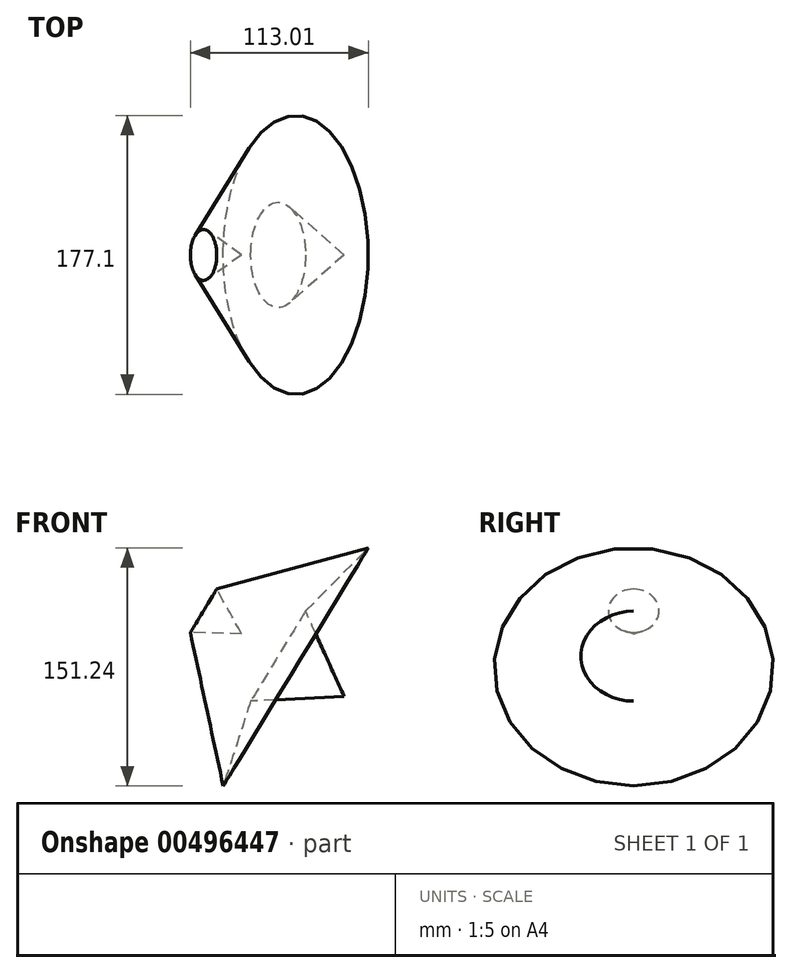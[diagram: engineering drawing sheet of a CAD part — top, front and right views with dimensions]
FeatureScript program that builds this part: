
annotation { "Feature Type Name" : "Feature", "Feature Type Description" : "" }
export const myFeature = defineFeature(function(context is Context, id is Id, definition is map)
    precondition{}
    {
        {
            var Q0;
            Q0=qCreatedBy(makeId("Front.planeOp"),FACE);
            var sketch = newSketch(context, id + "F0", { "sketchPlane" : qUnion([Q0])});
            skLineSegment(sketch, "E0", {"start": v(0, 0) * mm, "end": v(-15.85, 28.54) * mm});
            skLineSegment(sketch, "E1", {"start": v(-15.85, 28.54) * mm, "end": v(80.38, 54.72) * mm});
            skLineSegment(sketch, "E2", {"start": v(80.38, 54.72) * mm, "end": v(40.5, 14.5) * mm});
            skLineSegment(sketch, "E3", {"start": v(40.5, 14.5) * mm, "end": v(64.96, -39.58) * mm});
            skLineSegment(sketch, "E4", {"start": v(64.96, -39.58) * mm, "end": v(0, 0) * mm});
            skSolve(sketch);
        }
        {
            var Q0;
            Q0=makeQuery(id+"F0.imprint","IMPRINT",FACE,{"disambiguationData":[TD([[makeQuery(id+"F0.imprint","IMPRINT",EDGE,{"derivedFrom":sQuery(id+"F0.wireOp",EDGE,"E0")}),-1.0]])]});
            var Q1;
            Q1=sQuery(id+"F0.wireOp",EDGE,"E4");
            revolve(context, id + "F1", {"entities" : qUnion([Q0]), "axis" : qUnion([Q1]), "revolveType" : RevolveType.FULL});
        }
    });
